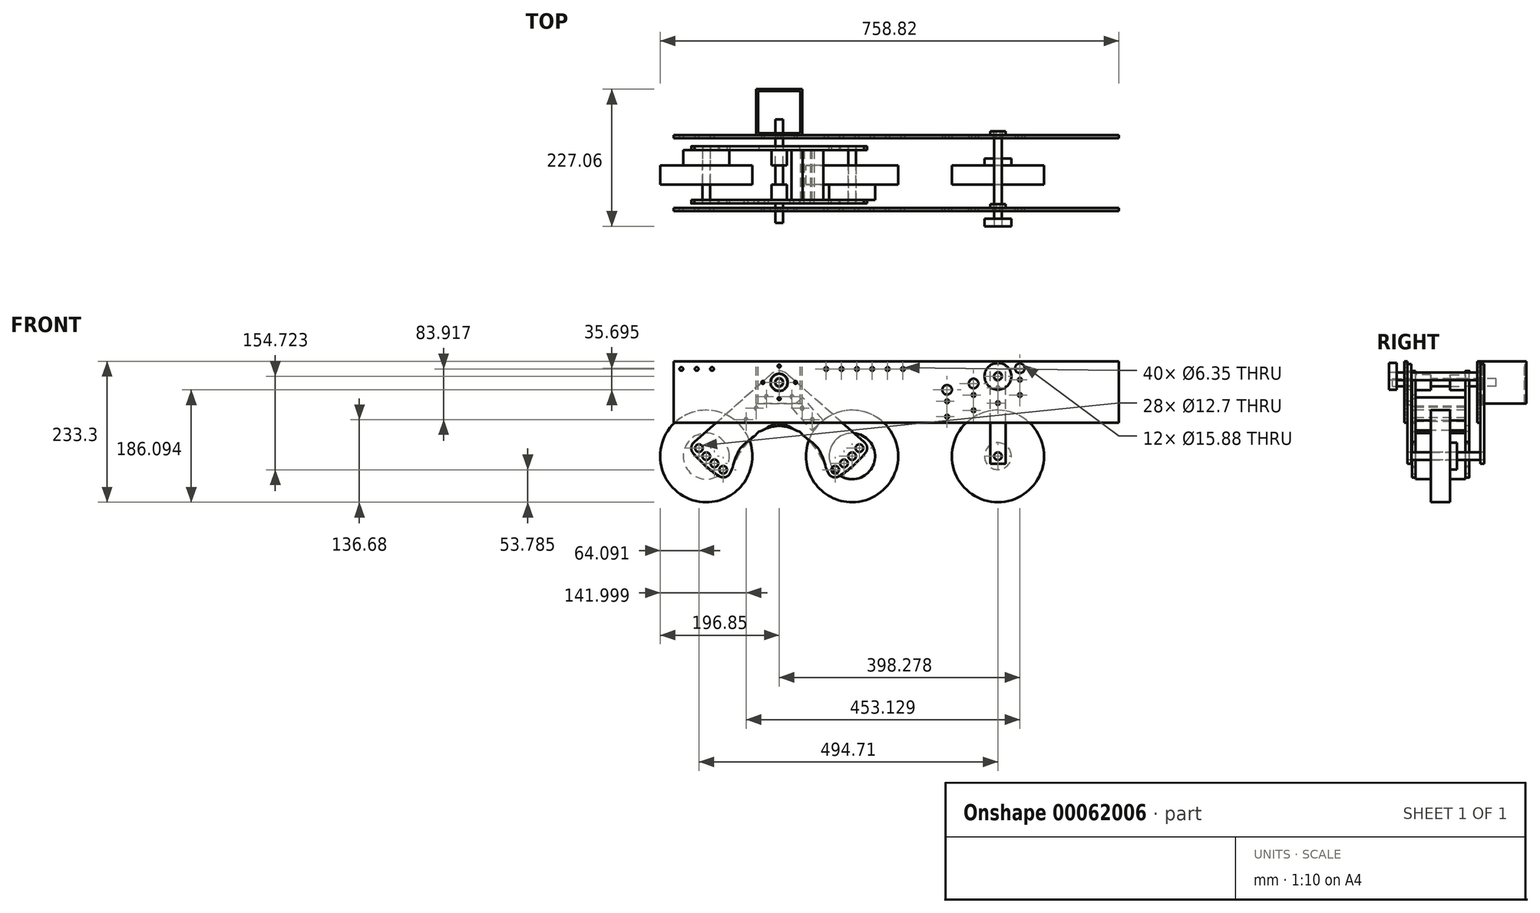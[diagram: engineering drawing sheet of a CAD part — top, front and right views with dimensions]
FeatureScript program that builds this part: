
annotation { "Feature Type Name" : "Feature", "Feature Type Description" : "" }
export const myFeature = defineFeature(function(context is Context, id is Id, definition is map)
    precondition{}
    {
        {
            var Q0;
            Q0=qCreatedBy(makeId("Front.planeOp"),FACE);
            var sketch = newSketch(context, id + "F0", { "sketchPlane" : qUnion([Q0])});
            skLineSegment(sketch, "E0", {"start": v(0, 0) * mm, "end": v(120.65, 122.17) * mm, "construction": true});
            skLineSegment(sketch, "E1", {"start": v(120.65, 122.17) * mm, "end": v(241.3, 0) * mm, "construction": true});
            skLineSegment(sketch, "E2", {"start": v(120.65, 122.17) * mm, "end": v(463.55, 122.17) * mm, "construction": true});
            skArc(sketch, "E3.0.startCap", {"start": v(120.65, 103.12) * mm, "mid": v(101.6, 122.17) * mm, "end": v(120.65, 141.22) * mm});
            skArc(sketch, "E3.0.endCap", {"start": v(463.55, 141.22) * mm, "mid": v(482.6, 122.17) * mm, "end": v(463.55, 103.12) * mm});
            skLineSegment(sketch, "E3.0.left", {"start": v(120.65, 141.22) * mm, "end": v(463.55, 141.22) * mm});
            skLineSegment(sketch, "E3.0.right", {"start": v(120.65, 103.12) * mm, "end": v(463.55, 103.12) * mm});
            skLineSegment(sketch, "E4", {"start": v(482.6, 132.33) * mm, "end": v(482.6, 0.02) * mm, "construction": true});
            skArc(sketch, "E5.0.startCap", {"start": v(469.9, 132.33) * mm, "mid": v(482.6, 145.03) * mm, "end": v(495.3, 132.33) * mm});
            skArc(sketch, "E5.0.endCap", {"start": v(495.3, 0.02) * mm, "mid": v(482.6, -12.68) * mm, "end": v(469.9, 0.02) * mm});
            skLineSegment(sketch, "E5.0.left", {"start": v(495.3, 132.33) * mm, "end": v(495.3, 0.02) * mm});
            skLineSegment(sketch, "E5.0.right", {"start": v(469.9, 132.33) * mm, "end": v(469.9, 0.02) * mm});
            skCircle(sketch, "E6", {"center": v(241.3, 0) * mm, "radius": 76.2 * mm});
            skCircle(sketch, "E7", {"center": v(0, 0) * mm, "radius": 76.2 * mm});
            skCircle(sketch, "E8", {"center": v(482.6, 0.02) * mm, "radius": 76.2 * mm});
            skCircle(sketch, "E9", {"center": v(0, 0) * mm, "radius": 6.35 * mm});
            skCircle(sketch, "E10", {"center": v(241.3, 0) * mm, "radius": 6.35 * mm});
            skCircle(sketch, "E11", {"center": v(482.6, 0.02) * mm, "radius": 6.35 * mm});
            skCircle(sketch, "E12", {"center": v(120.65, 122.17) * mm, "radius": 6.35 * mm});
            skCircle(sketch, "E13", {"center": v(0, 0) * mm, "radius": 38.1 * mm});
            skCircle(sketch, "E14", {"center": v(120.65, 122.17) * mm, "radius": 171.7 * mm, "construction": true});
            skCircle(sketch, "E15", {"center": v(13.43, -11.94) * mm, "radius": 6.35 * mm});
            skCircle(sketch, "E16", {"center": v(227.87, -11.94) * mm, "radius": 6.35 * mm});
            skCircle(sketch, "E17", {"center": v(213.26, -22.41) * mm, "radius": 6.35 * mm});
            skCircle(sketch, "E18", {"center": v(28.04, -22.41) * mm, "radius": 6.35 * mm});
            skLineSegment(sketch, "E19", {"start": v(13.43, -11.94) * mm, "end": v(120.65, 122.17) * mm, "construction": true});
            skLineSegment(sketch, "E20", {"start": v(120.65, 122.17) * mm, "end": v(28.04, -22.41) * mm, "construction": true});
            skLineSegment(sketch, "E21", {"start": v(120.65, 122.17) * mm, "end": v(213.26, -22.41) * mm, "construction": true});
            skLineSegment(sketch, "E22", {"start": v(120.65, 122.17) * mm, "end": v(227.87, -11.94) * mm, "construction": true});
            skLineSegment(sketch, "E23", {"start": v(120.65, 122.17) * mm, "end": v(253.4, 13.28) * mm, "construction": true});
            skLineSegment(sketch, "E24", {"start": v(120.65, 122.17) * mm, "end": v(-12.1, 13.28) * mm, "construction": true});
            skCircle(sketch, "E25", {"center": v(253.4, 13.28) * mm, "radius": 6.35 * mm});
            skCircle(sketch, "E26", {"center": v(-12.1, 13.28) * mm, "radius": 6.35 * mm});
            skCircle(sketch, "E27", {"center": v(120.65, 122.17) * mm, "radius": 19.05 * mm});
            skCircle(sketch, "E28", {"center": v(253.4, 13.28) * mm, "radius": 12.7 * mm, "construction": true});
            skLineSegment(sketch, "E29", {"start": v(261.1, 23.4) * mm, "end": v(133.27, 136.44) * mm});
            skCircle(sketch, "E30", {"center": v(-12.1, 13.28) * mm, "radius": 12.7 * mm, "construction": true});
            skLineSegment(sketch, "E31", {"start": v(120.65, 122.17) * mm, "end": v(263.23, 5.23) * mm, "construction": true});
            skArc(sketch, "E32", {"start": v(263.23, 5.23) * mm, "mid": v(120.65, -62.23) * mm, "end": v(-21.93, 5.23) * mm});
            skCircle(sketch, "E33", {"center": v(213.26, -22.41) * mm, "radius": 12.7 * mm, "construction": true});
            skCircle(sketch, "E34", {"center": v(28.04, -22.41) * mm, "radius": 12.7 * mm, "construction": true});
            skLineSegment(sketch, "E35", {"start": v(202.32, -28.86) * mm, "end": v(105, 111.3) * mm});
            skLineSegment(sketch, "E36", {"start": v(38.98, -28.86) * mm, "end": v(136.3, 111.3) * mm});
            skLineSegment(sketch, "E37", {"start": v(-19.8, 23.4) * mm, "end": v(108.03, 136.44) * mm});
            skLineSegment(sketch, "E38", {"start": v(303.84, -76.2) * mm, "end": v(-84, -76.2) * mm, "construction": true});
            skLineSegment(sketch, "E39", {"start": v(121.32, -76.2) * mm, "end": v(121.32, 40.64) * mm, "construction": true});
            skLineSegment(sketch, "E40", {"start": v(154.07, 40.64) * mm, "end": v(87.23, 40.64) * mm});
            skLineSegment(sketch, "E41.bottom", {"start": v(-53.97, 157.1) * mm, "end": v(682.62, 157.1) * mm});
            skLineSegment(sketch, "E41.top", {"start": v(-53.97, 55.5) * mm, "end": v(682.62, 55.5) * mm});
            skLineSegment(sketch, "E41.left", {"start": v(-53.98, 157.1) * mm, "end": v(-53.98, 55.5) * mm});
            skLineSegment(sketch, "E41.right", {"start": v(682.62, 157.1) * mm, "end": v(682.62, 55.5) * mm});
            skLineSegment(sketch, "E42", {"start": v(28.04, -22.41) * mm, "end": v(398.49, -22.41) * mm, "construction": true});
            skLineSegment(sketch, "E43", {"start": v(13.43, -11.94) * mm, "end": v(442.3, -11.94) * mm, "construction": true});
            skLineSegment(sketch, "E44", {"start": v(-12.1, 13.28) * mm, "end": v(518.93, 13.28) * mm, "construction": true});
            skLineSegment(sketch, "E45", {"start": v(398.49, -22.41) * mm, "end": v(398.49, 109.9) * mm, "construction": true});
            skLineSegment(sketch, "E46", {"start": v(442.3, -11.94) * mm, "end": v(442.3, 120.37) * mm, "construction": true});
            skLineSegment(sketch, "E47", {"start": v(518.93, 13.28) * mm, "end": v(518.93, 145.59) * mm, "construction": true});
            skLineSegment(sketch, "E48", {"start": v(0, 0) * mm, "end": v(482.6, 0) * mm, "construction": true});
            skLineSegment(sketch, "E49", {"start": v(482.6, 0) * mm, "end": v(482.6, 132.3) * mm, "construction": true});
            skSolve(sketch);
        }
        {
            var Q0;
            Q0=qCreatedBy(makeId("Front.planeOp"),FACE);
            var sketch = newSketch(context, id + "F1", { "sketchPlane" : qUnion([Q0])});
            skCircle(sketch, "E50.0", {"center": v(0, 0) * mm, "radius": 76.2 * mm});
            skCircle(sketch, "E51.0", {"center": v(241.3, 0) * mm, "radius": 76.2 * mm});
            skCircle(sketch, "E52.0", {"center": v(0, 0) * mm, "radius": 6.35 * mm});
            skCircle(sketch, "E53.0", {"center": v(241.3, 0) * mm, "radius": 6.35 * mm});
            skCircle(sketch, "E54.0", {"center": v(482.6, 0.02) * mm, "radius": 76.2 * mm});
            skCircle(sketch, "E55.0", {"center": v(482.6, 0.02) * mm, "radius": 6.35 * mm});
            skSolve(sketch);
        }
        {
            var Q0;
            Q0=makeQuery(id+"F1.imprint","IMPRINT",FACE,{"disambiguationData":[TD([[makeQuery(id+"F1.imprint","IMPRINT",EDGE,{"derivedFrom":sQuery(id+"F1.wireOp",EDGE,"E50.0")}),1.0]])]});
            var Q1;
            Q1=makeQuery(id+"F1.imprint","IMPRINT",FACE,{"disambiguationData":[TD([[makeQuery(id+"F1.imprint","IMPRINT",EDGE,{"derivedFrom":sQuery(id+"F1.wireOp",EDGE,"E51.0")}),1.0]])]});
            var Q2;
            Q2=makeQuery(id+"F1.imprint","IMPRINT",FACE,{"disambiguationData":[TD([[makeQuery(id+"F1.imprint","IMPRINT",EDGE,{"derivedFrom":sQuery(id+"F1.wireOp",EDGE,"E54.0")}),1.0]])]});
            extrude(context, id + "F2", {"entities" : qUnion([Q0, Q1, Q2]), "depth" : 31.75 * mm});
        }
        {
            var Q0;
            {var subQ0=sQuery(id+"F0.wireOp",EDGE,"E37");var subQ1=sQuery(id+"F0.wireOp",EDGE,"E7");var subQ2=makeQuery(id+"F0.imprint","INTERSECT",VERTEX,{"derivedFrom":[subQ1,subQ0]});Q0=makeQuery(id+"F0.imprint","IMPRINT",FACE,{"disambiguationData":[TD([[makeQuery(id+"F0.imprint","IMPRINT",EDGE,{"disambiguationData":[TD([[subQ2,-1.0]])],"derivedFrom":subQ1}),1.0]])]});}
            var sketch = newSketch(context, id + "F3", { "sketchPlane" : qUnion([Q0])});
            skCircle(sketch, "E56.0", {"center": v(0, 0) * mm, "radius": 38.1 * mm});
            skCircle(sketch, "E57.0", {"center": v(0, 0) * mm, "radius": 6.35 * mm});
            skSolve(sketch);
        }
        {
            var Q0;
            Q0=qSketchRegion(id+"F3",true);
            extrude(context, id + "F4", {"entities" : qUnion([Q0]), "oppositeDirection" : true, "depth" : 25.4 * mm});
        }
        {
            var Q0;
            Q0=makeQuery(id+"F2.opExtrude","CAP_FACE",FACE,{"disambiguationData":[OSD([sQuery(id+"F1.wireOp",EDGE,"E51.0")])],"isStart":false});
            var sketch = newSketch(context, id + "F5", { "sketchPlane" : qUnion([Q0])});
            skPoint(sketch, "E58.0", {"position": v(241.3, 0) * mm});
            skCircle(sketch, "E59", {"center": v(241.3, 0) * mm, "radius": 38.1 * mm});
            skCircle(sketch, "E60.0", {"center": v(241.3, 0) * mm, "radius": 6.35 * mm});
            skSolve(sketch);
        }
        {
            var Q0;
            Q0=qSketchRegion(id+"F5",true);
            extrude(context, id + "F6", {"entities" : qUnion([Q0]), "depth" : 25.4 * mm});
        }
        {
            var Q0;
            Q0=makeQuery(id+"F0.imprint","IMPRINT",FACE,{"disambiguationData":[TD([[makeQuery(id+"F0.imprint","IMPRINT",EDGE,{"derivedFrom":sQuery(id+"F0.wireOp",EDGE,"E12")}),1.0]])]});
            var Q1;
            Q1=makeQuery(id+"F4.opExtrude","CAP_FACE",FACE,{"disambiguationData":[OSD([sQuery(id+"F3.wireOp",EDGE,"E56.0")])],"isStart":false});
            var Q2;
            Q2=makeQuery(id+"F6.opExtrude","CAP_FACE",FACE,{"disambiguationData":[OSD([sQuery(id+"F5.wireOp",EDGE,"E59")])],"isStart":false});
            extrude(context, id + "F7", {"entities" : qUnion([Q0]), "endBound" : BoundingType.UP_TO_SURFACE, "oppositeDirection" : true, "endBoundEntityFace" : qUnion([Q1]), "depth" : 25.4 * mm, "hasSecondDirection" : true, "secondDirectionBound" : BoundingType.UP_TO_SURFACE, "secondDirectionOppositeDirection" : false, "secondDirectionBoundEntityFace" : qUnion([Q2]), "secondDirectionDepth" : 25.4 * mm});
        }
        {
            var Q0;
            Q0=makeQuery(id+"F7.opExtrude","CAP_FACE",FACE,{"disambiguationData":[OSD([sQuery(id+"F0.wireOp",EDGE,"E12")])],"isStart":true});
            var sketch = newSketch(context, id + "F8", { "sketchPlane" : qUnion([Q0])});
            skCircle(sketch, "E61", {"center": v(120.65, 122.17) * mm, "radius": 12.7 * mm});
            skSolve(sketch);
        }
        {
            var Q0;
            Q0=makeQuery(id+"F8.imprint","IMPRINT",FACE,{"disambiguationData":[TD([[makeQuery(id+"F8.imprint","IMPRINT",EDGE,{"derivedFrom":sQuery(id+"F8.wireOp",EDGE,"E61")}),1.0]])]});
            extrude(context, id + "F9", {"entities" : qUnion([Q0]), "oppositeDirection" : true, "depth" : 25.4 * mm});
        }
        {
            var Q0;
            Q0=makeQuery(id+"F7.opExtrude","CAP_FACE",FACE,{"disambiguationData":[OSD([sQuery(id+"F0.wireOp",EDGE,"E12")])],"isStart":false});
            var sketch = newSketch(context, id + "F10", { "sketchPlane" : qUnion([Q0])});
            skCircle(sketch, "E62.0", {"center": v(-120.65, 122.17) * mm, "radius": 12.7 * mm});
            skSolve(sketch);
        }
        {
            var Q0;
            Q0=makeQuery(id+"F10.imprint","IMPRINT",FACE,{"disambiguationData":[TD([[makeQuery(id+"F10.imprint","IMPRINT",EDGE,{"derivedFrom":sQuery(id+"F10.wireOp",EDGE,"E62.0")}),1.0]])]});
            extrude(context, id + "F11", {"entities" : qUnion([Q0]), "oppositeDirection" : true, "depth" : 25.4 * mm});
        }
        {
            var Q0;
            Q0=makeQuery(id+"F4.opExtrude","CAP_FACE",FACE,{"disambiguationData":[OSD([sQuery(id+"F3.wireOp",EDGE,"E56.0"),sQuery(id+"F3.wireOp",EDGE,"E57.0")])],"isStart":false});
            var sketch = newSketch(context, id + "F12", { "sketchPlane" : qUnion([Q0])});
            skLineSegment(sketch, "E63.0", {"start": v(-261.1, 23.4) * mm, "end": v(-133.27, 136.44) * mm});
            skArc(sketch, "E64.0", {"start": v(-133.27, 136.44) * mm, "mid": v(-120.65, 141.22) * mm, "end": v(-108.03, 136.44) * mm});
            skLineSegment(sketch, "E65.0", {"start": v(19.8, 23.4) * mm, "end": v(-108.03, 136.44) * mm});
            skLineSegment(sketch, "E66.0", {"start": v(-202.32, -28.86) * mm, "end": v(-154.07, 40.64) * mm, "construction": true});
            skLineSegment(sketch, "E67.0", {"start": v(-38.98, -28.86) * mm, "end": v(-87.23, 40.64) * mm, "construction": true});
            skLineSegment(sketch, "E68.0", {"start": v(-154.07, 40.64) * mm, "end": v(-87.23, 40.64) * mm, "construction": true});
            skArc(sketch, "E69.0", {"start": v(-202.32, -28.86) * mm, "mid": v(-210.32, -34.77) * mm, "end": v(-220.11, -33.1) * mm});
            skArc(sketch, "E70.0", {"start": v(-263.23, 5.23) * mm, "mid": v(-243.18, -15.64) * mm, "end": v(-220.11, -33.1) * mm});
            skArc(sketch, "E71.0", {"start": v(-263.23, 5.23) * mm, "mid": v(-266.02, 14.76) * mm, "end": v(-261.1, 23.4) * mm});
            skCircle(sketch, "E72.0", {"center": v(-253.4, 13.28) * mm, "radius": 6.35 * mm});
            skCircle(sketch, "E73.0", {"center": v(-241.3, 0) * mm, "radius": 6.35 * mm});
            skCircle(sketch, "E74.0", {"center": v(-227.87, -11.94) * mm, "radius": 6.35 * mm});
            skCircle(sketch, "E75.0", {"center": v(-213.26, -22.41) * mm, "radius": 6.35 * mm});
            skCircle(sketch, "E76.0", {"center": v(-120.65, 122.17) * mm, "radius": 6.35 * mm});
            skCircle(sketch, "E77.0", {"center": v(-28.04, -22.41) * mm, "radius": 6.35 * mm});
            skCircle(sketch, "E78.0", {"center": v(-13.43, -11.94) * mm, "radius": 6.35 * mm});
            skCircle(sketch, "E79.0", {"center": v(0, 0) * mm, "radius": 6.35 * mm});
            skCircle(sketch, "E80.0", {"center": v(12.1, 13.28) * mm, "radius": 6.35 * mm});
            skArc(sketch, "E81.0", {"start": v(19.8, 23.4) * mm, "mid": v(24.72, 14.76) * mm, "end": v(21.93, 5.23) * mm});
            skArc(sketch, "E82.trimOffspring", {"start": v(-21.19, -33.1) * mm, "mid": v(1.88, -15.64) * mm, "end": v(21.93, 5.23) * mm});
            skPoint(sketch, "E83.trimOffspring.end.orphan", {"position": v(-105, 111.3) * mm});
            skPoint(sketch, "E84.trimOffspring.end.orphan", {"position": v(-136.3, 111.3) * mm});
            skPoint(sketch, "E85", {"position": v(-120.65, 40.64) * mm});
            skLineSegment(sketch, "E86", {"start": v(-120.65, 40.64) * mm, "end": v(-120.65, 50.16) * mm, "construction": true});
            skFitSpline(sketch, "E87", {"points": [v(-154.07, 40.64) * mm, v(-120.65, 50.16) * mm, v(-87.23, 40.64) * mm], "startDerivative": vector(66.83, 28.57) * mm, "endDerivative": vector(66.83, -28.58) * mm});
            skArc(sketch, "E88", {"start": v(-38.98, -28.86) * mm, "mid": v(-30.98, -34.77) * mm, "end": v(-21.19, -33.1) * mm});
            skLineSegment(sketch, "E89", {"start": v(-178.2, 5.89) * mm, "end": v(-183.41, 9.5) * mm, "construction": true});
            skLineSegment(sketch, "E90", {"start": v(-63.1, 5.89) * mm, "end": v(-57.89, 9.5) * mm, "construction": true});
            skFitSpline(sketch, "E91", {"points": [v(-202.32, -28.86) * mm, v(-183.41, 9.5) * mm, v(-154.07, 40.64) * mm], "startDerivative": vector(32.6, 80.37) * mm, "endDerivative": vector(63.9, 58.64) * mm});
            skFitSpline(sketch, "E92", {"points": [v(-87.23, 40.64) * mm, v(-57.89, 9.5) * mm, v(-38.98, -28.86) * mm], "startDerivative": vector(63.9, -58.64) * mm, "endDerivative": vector(32.6, -80.37) * mm});
            skSolve(sketch);
        }
        {
            var Q0;
            Q0=qSketchRegion(id+"F12",true);
            extrude(context, id + "F13", {"entities" : qUnion([Q0]), "depth" : 6.05 * mm});
        }
        {
            var Q0;
            Q0=makeQuery(id+"F6.opExtrude","CAP_FACE",FACE,{"disambiguationData":[OSD([sQuery(id+"F5.wireOp",EDGE,"E59")])],"isStart":false});
            var sketch = newSketch(context, id + "F14", { "sketchPlane" : qUnion([Q0])});
            skLineSegment(sketch, "E93.0.0", {"start": v(108.03, 136.44) * mm, "end": v(-19.8, 23.4) * mm});
            skArc(sketch, "E93.0.1", {"start": v(-19.8, 23.4) * mm, "mid": v(-24.72, 14.76) * mm, "end": v(-21.93, 5.23) * mm});
            skArc(sketch, "E93.0.2", {"start": v(-21.93, 5.23) * mm, "mid": v(-1.88, -15.64) * mm, "end": v(21.19, -33.1) * mm});
            skArc(sketch, "E93.0.3", {"start": v(21.19, -33.1) * mm, "mid": v(30.98, -34.77) * mm, "end": v(38.98, -28.86) * mm});
            skFitSpline(sketch, "E93.0.4", {"points": [v(38.98, -28.86) * mm, v(44.41, -15.47) * mm, v(55.28, 11.32) * mm, v(76.58, 30.87) * mm, v(87.23, 40.64) * mm]});
            skFitSpline(sketch, "E93.0.5", {"points": [v(87.23, 40.64) * mm, v(98.37, 45.4) * mm, v(120.65, 54.93) * mm, v(142.93, 45.4) * mm, v(154.07, 40.64) * mm]});
            skFitSpline(sketch, "E93.0.6", {"points": [v(154.07, 40.64) * mm, v(164.72, 30.87) * mm, v(186.02, 11.32) * mm, v(196.89, -15.47) * mm, v(202.32, -28.86) * mm]});
            skArc(sketch, "E93.0.7", {"start": v(202.32, -28.86) * mm, "mid": v(210.32, -34.77) * mm, "end": v(220.11, -33.1) * mm});
            skArc(sketch, "E93.0.8", {"start": v(220.11, -33.1) * mm, "mid": v(243.18, -15.64) * mm, "end": v(263.23, 5.23) * mm});
            skArc(sketch, "E93.0.9", {"start": v(263.23, 5.23) * mm, "mid": v(266.02, 14.76) * mm, "end": v(261.1, 23.4) * mm});
            skLineSegment(sketch, "E93.0.10", {"start": v(261.1, 23.4) * mm, "end": v(133.27, 136.44) * mm});
            skArc(sketch, "E93.0.11", {"start": v(133.27, 136.44) * mm, "mid": v(120.65, 141.22) * mm, "end": v(108.03, 136.44) * mm});
            skCircle(sketch, "E94.0", {"center": v(-12.1, 13.28) * mm, "radius": 6.35 * mm});
            skCircle(sketch, "E95.0", {"center": v(0, 0) * mm, "radius": 6.35 * mm});
            skCircle(sketch, "E96.0", {"center": v(13.43, -11.94) * mm, "radius": 6.35 * mm});
            skCircle(sketch, "E97.0", {"center": v(28.04, -22.41) * mm, "radius": 6.35 * mm});
            skCircle(sketch, "E98.0", {"center": v(120.65, 122.17) * mm, "radius": 6.35 * mm});
            skCircle(sketch, "E99.0", {"center": v(213.26, -22.41) * mm, "radius": 6.35 * mm});
            skCircle(sketch, "E100.0", {"center": v(227.87, -11.94) * mm, "radius": 6.35 * mm});
            skCircle(sketch, "E101.0", {"center": v(241.3, 0) * mm, "radius": 6.35 * mm});
            skCircle(sketch, "E102.0", {"center": v(253.4, 13.28) * mm, "radius": 6.35 * mm});
            skCircle(sketch, "E103.0", {"center": v(120.65, 122.17) * mm, "radius": 12.7 * mm, "construction": true});
            skCircle(sketch, "E104", {"center": v(28.04, -22.41) * mm, "radius": 38.1 * mm, "construction": true});
            skCircle(sketch, "E105", {"center": v(-12.1, 13.28) * mm, "radius": 38.1 * mm, "construction": true});
            skLineSegment(sketch, "E106", {"start": v(16.14, -12.28) * mm, "end": v(131.4, 115.12) * mm, "construction": true});
            skLineSegment(sketch, "E107", {"start": v(-0.65, 2.66) * mm, "end": v(111.09, 130.53) * mm, "construction": true});
            skLineSegment(sketch, "E108", {"start": v(120.65, 122.17) * mm, "end": v(42.47, 34.24) * mm, "construction": true});
            skLineSegment(sketch, "E109", {"start": v(33.67, 41.93) * mm, "end": v(51.27, 26.55) * mm, "construction": true});
            skCircle(sketch, "E110", {"center": v(99.55, 98.44) * mm, "radius": 3.18 * mm});
            skCircle(sketch, "E111", {"center": v(82.68, 79.46) * mm, "radius": 3.18 * mm});
            skPoint(sketch, "E112.centerSnap0", {"position": v(55.22, 66.6) * mm});
            skCircle(sketch, "E113", {"center": v(65.8, 60.48) * mm, "radius": 3.18 * mm});
            skLineSegment(sketch, "E114", {"start": v(120.65, 122.17) * mm, "end": v(120.65, 50.16) * mm, "construction": true});
            skCircle(sketch, "E115.MirrorC", {"center": v(141.75, 98.44) * mm, "radius": 3.18 * mm});
            skCircle(sketch, "E116.MirrorC", {"center": v(158.62, 79.46) * mm, "radius": 3.18 * mm});
            skCircle(sketch, "E117.MirrorC", {"center": v(175.5, 60.48) * mm, "radius": 3.18 * mm});
            skSolve(sketch);
        }
        {
            var Q0;
            Q0=qSketchRegion(id+"F14",true);
            extrude(context, id + "F15", {"entities" : qUnion([Q0]), "depth" : 6.05 * mm});
        }
        {
            var Q0;
            Q0=makeQuery(id+"F15.opExtrude","CAP_FACE",FACE,{"disambiguationData":[OSD([sQuery(id+"F14.wireOp",EDGE,"E93.0.0"),sQuery(id+"F14.wireOp",EDGE,"E93.0.1"),sQuery(id+"F14.wireOp",EDGE,"E93.0.2"),sQuery(id+"F14.wireOp",EDGE,"E93.0.3"),sQuery(id+"F14.wireOp",EDGE,"E93.0.4"),sQuery(id+"F14.wireOp",EDGE,"E93.0.5"),sQuery(id+"F14.wireOp",EDGE,"E93.0.6"),sQuery(id+"F14.wireOp",EDGE,"E93.0.7"),sQuery(id+"F14.wireOp",EDGE,"E93.0.8"),sQuery(id+"F14.wireOp",EDGE,"E93.0.9"),sQuery(id+"F14.wireOp",EDGE,"E93.0.10"),sQuery(id+"F14.wireOp",EDGE,"E93.0.11"),sQuery(id+"F14.wireOp",EDGE,"E94.0"),sQuery(id+"F14.wireOp",EDGE,"E95.0"),sQuery(id+"F14.wireOp",EDGE,"E96.0"),sQuery(id+"F14.wireOp",EDGE,"E97.0"),sQuery(id+"F14.wireOp",EDGE,"E98.0"),sQuery(id+"F14.wireOp",EDGE,"E99.0"),sQuery(id+"F14.wireOp",EDGE,"E100.0"),sQuery(id+"F14.wireOp",EDGE,"E101.0"),sQuery(id+"F14.wireOp",EDGE,"E102.0"),sQuery(id+"F14.wireOp",EDGE,"E110"),sQuery(id+"F14.wireOp",EDGE,"E111"),sQuery(id+"F14.wireOp",EDGE,"E113"),sQuery(id+"F14.wireOp",EDGE,"E115.MirrorC"),sQuery(id+"F14.wireOp",EDGE,"E116.MirrorC"),sQuery(id+"F14.wireOp",EDGE,"E117.MirrorC")])],"isStart":false});
            cPlane(context, id + "F16", {"entities" : qUnion([Q0]), "cplaneType" : CPlaneType.OFFSET, "offset" : 107.95 * mm, "oppositeDirection" : true, "width" : 152.4 * mm, "height" : 152.4 * mm});
        }
        {
            var Q0;
            Q0=qCreatedBy(makeId("Right.planeOp"),FACE);
            var Q1;
            Q1=sQuery(id+"F12.wireOp",VERTEX,"E64.0.center");
            cPlane(context, id + "F17", {"entities" : qUnion([Q0, Q1]), "cplaneType" : CPlaneType.PLANE_POINT, "offset" : 152.4 * mm, "width" : 152.4 * mm, "height" : 152.4 * mm});
        }
        {
            var Q0;
            Q0=qCreatedBy(id+"F16.planeOp",FACE);
            var sketch = newSketch(context, id + "F18", { "sketchPlane" : qUnion([Q0])});
            skLineSegment(sketch, "E118.0", {"start": v(-53.97, 55.5) * mm, "end": v(682.62, 55.5) * mm});
            skLineSegment(sketch, "E119.0", {"start": v(-53.98, 157.1) * mm, "end": v(-53.98, 55.5) * mm});
            skLineSegment(sketch, "E120.0", {"start": v(-53.97, 157.1) * mm, "end": v(682.62, 157.1) * mm});
            skLineSegment(sketch, "E121.0", {"start": v(682.62, 157.1) * mm, "end": v(682.62, 55.5) * mm});
            skCircle(sketch, "E122.0", {"center": v(120.65, 122.17) * mm, "radius": 6.35 * mm});
            skLineSegment(sketch, "E123.rect.bottom", {"start": v(147.64, 149.16) * mm, "end": v(93.66, 149.16) * mm, "construction": true});
            skLineSegment(sketch, "E123.rect.top", {"start": v(147.64, 95.18) * mm, "end": v(93.66, 95.18) * mm, "construction": true});
            skLineSegment(sketch, "E123.rect.left", {"start": v(147.64, 149.16) * mm, "end": v(147.64, 95.18) * mm, "construction": true});
            skLineSegment(sketch, "E123.rect.right", {"start": v(93.66, 149.16) * mm, "end": v(93.66, 95.18) * mm, "construction": true});
            skCircle(sketch, "E124", {"center": v(120.65, 149.16) * mm, "radius": 2.43 * mm});
            skCircle(sketch, "E125", {"center": v(147.64, 122.17) * mm, "radius": 2.43 * mm});
            skCircle(sketch, "E126", {"center": v(120.65, 95.18) * mm, "radius": 2.43 * mm});
            skCircle(sketch, "E127", {"center": v(93.66, 122.17) * mm, "radius": 2.43 * mm});
            skPoint(sketch, "E128.0", {"position": v(518.93, 145.59) * mm});
            skPoint(sketch, "E129.0", {"position": v(482.6, 132.3) * mm});
            skPoint(sketch, "E130.0", {"position": v(442.3, 120.37) * mm});
            skPoint(sketch, "E131.0", {"position": v(398.49, 109.9) * mm});
            skCircle(sketch, "E132", {"center": v(518.93, 145.59) * mm, "radius": 7.94 * mm});
            skCircle(sketch, "E133", {"center": v(482.6, 132.3) * mm, "radius": 7.94 * mm});
            skCircle(sketch, "E134", {"center": v(442.3, 120.37) * mm, "radius": 7.94 * mm});
            skCircle(sketch, "E135", {"center": v(398.49, 109.9) * mm, "radius": 7.94 * mm});
            skLineSegment(sketch, "E136", {"start": v(518.93, 145.59) * mm, "end": v(518.93, 126.54) * mm, "construction": true});
            skPoint(sketch, "E137", {"position": v(482.6, 113.26) * mm});
            skPoint(sketch, "E138", {"position": v(442.3, 101.32) * mm});
            skPoint(sketch, "E139", {"position": v(398.49, 90.84) * mm});
            skLineSegment(sketch, "E140", {"start": v(482.6, 113.26) * mm, "end": v(482.6, 132.3) * mm, "construction": true});
            skLineSegment(sketch, "E141", {"start": v(442.3, 101.32) * mm, "end": v(442.3, 120.37) * mm, "construction": true});
            skLineSegment(sketch, "E142", {"start": v(398.49, 90.84) * mm, "end": v(398.49, 109.9) * mm, "construction": true});
            skPoint(sketch, "E143", {"position": v(518.93, 101.14) * mm});
            skPoint(sketch, "E144", {"position": v(482.6, 87.86) * mm});
            skPoint(sketch, "E145", {"position": v(442.3, 75.92) * mm});
            skPoint(sketch, "E146", {"position": v(398.49, 65.44) * mm});
            skLineSegment(sketch, "E147", {"start": v(518.93, 126.54) * mm, "end": v(518.93, 101.14) * mm, "construction": true});
            skLineSegment(sketch, "E148", {"start": v(482.6, 87.86) * mm, "end": v(482.6, 113.26) * mm, "construction": true});
            skLineSegment(sketch, "E149", {"start": v(442.3, 75.92) * mm, "end": v(442.3, 101.32) * mm, "construction": true});
            skLineSegment(sketch, "E150", {"start": v(398.49, 65.44) * mm, "end": v(398.49, 90.84) * mm, "construction": true});
            skCircle(sketch, "E151", {"center": v(518.93, 126.54) * mm, "radius": 3.18 * mm});
            skCircle(sketch, "E152", {"center": v(518.93, 101.14) * mm, "radius": 3.18 * mm});
            skCircle(sketch, "E153", {"center": v(482.6, 113.26) * mm, "radius": 3.18 * mm});
            skCircle(sketch, "E154", {"center": v(482.6, 87.86) * mm, "radius": 3.18 * mm});
            skCircle(sketch, "E155", {"center": v(442.3, 101.32) * mm, "radius": 3.17 * mm});
            skCircle(sketch, "E156", {"center": v(442.3, 75.92) * mm, "radius": 3.18 * mm});
            skCircle(sketch, "E157", {"center": v(398.49, 90.84) * mm, "radius": 3.18 * mm});
            skCircle(sketch, "E158", {"center": v(398.49, 65.44) * mm, "radius": 3.18 * mm});
            skCircle(sketch, "E159", {"center": v(-41.28, 144.4) * mm, "radius": 2.98 * mm});
            skCircle(sketch, "E160.1.0.0", {"center": v(-15.88, 144.4) * mm, "radius": 2.98 * mm});
            skCircle(sketch, "E160.2.0.0", {"center": v(9.52, 144.4) * mm, "radius": 2.98 * mm});
            skLineSegment(sketch, "E160.direction1", {"start": v(-41.28, 144.4) * mm, "end": v(-15.88, 144.4) * mm, "construction": true});
            skCircle(sketch, "E161", {"center": v(198.44, 144.4) * mm, "radius": 3.18 * mm});
            skCircle(sketch, "E162.1.0.0", {"center": v(223.84, 144.4) * mm, "radius": 3.18 * mm});
            skCircle(sketch, "E162.2.0.0", {"center": v(249.24, 144.4) * mm, "radius": 3.18 * mm});
            skCircle(sketch, "E162.3.0.0", {"center": v(274.64, 144.4) * mm, "radius": 3.18 * mm});
            skCircle(sketch, "E162.4.0.0", {"center": v(300.04, 144.4) * mm, "radius": 3.18 * mm});
            skCircle(sketch, "E162.5.0.0", {"center": v(325.44, 144.4) * mm, "radius": 3.18 * mm});
            skLineSegment(sketch, "E162.direction1", {"start": v(198.44, 144.4) * mm, "end": v(223.84, 144.4) * mm, "construction": true});
            skSolve(sketch);
        }
        {
            var Q0;
            Q0=qSketchRegion(id+"F18",true);
            extrude(context, id + "F19", {"entities" : qUnion([Q0]), "oppositeDirection" : true, "depth" : 4.94 * mm});
        }
        {
            var Q0;
            Q0=makeQuery(id+"F15.opExtrude","CAP_FACE",FACE,{"disambiguationData":[OSD([sQuery(id+"F14.wireOp",EDGE,"E93.0.0"),sQuery(id+"F14.wireOp",EDGE,"E93.0.1"),sQuery(id+"F14.wireOp",EDGE,"E93.0.2"),sQuery(id+"F14.wireOp",EDGE,"E93.0.3"),sQuery(id+"F14.wireOp",EDGE,"E93.0.4"),sQuery(id+"F14.wireOp",EDGE,"E93.0.5"),sQuery(id+"F14.wireOp",EDGE,"E93.0.6"),sQuery(id+"F14.wireOp",EDGE,"E93.0.7"),sQuery(id+"F14.wireOp",EDGE,"E93.0.8"),sQuery(id+"F14.wireOp",EDGE,"E93.0.9"),sQuery(id+"F14.wireOp",EDGE,"E93.0.10"),sQuery(id+"F14.wireOp",EDGE,"E93.0.11"),sQuery(id+"F14.wireOp",EDGE,"E94.0"),sQuery(id+"F14.wireOp",EDGE,"E95.0"),sQuery(id+"F14.wireOp",EDGE,"E96.0"),sQuery(id+"F14.wireOp",EDGE,"E97.0"),sQuery(id+"F14.wireOp",EDGE,"E98.0"),sQuery(id+"F14.wireOp",EDGE,"E99.0"),sQuery(id+"F14.wireOp",EDGE,"E100.0"),sQuery(id+"F14.wireOp",EDGE,"E101.0"),sQuery(id+"F14.wireOp",EDGE,"E102.0"),sQuery(id+"F14.wireOp",EDGE,"E110"),sQuery(id+"F14.wireOp",EDGE,"E111"),sQuery(id+"F14.wireOp",EDGE,"E113"),sQuery(id+"F14.wireOp",EDGE,"E115.MirrorC"),sQuery(id+"F14.wireOp",EDGE,"E116.MirrorC"),sQuery(id+"F14.wireOp",EDGE,"E117.MirrorC")])],"isStart":false});
            cPlane(context, id + "F20", {"entities" : qUnion([Q0]), "cplaneType" : CPlaneType.OFFSET, "offset" : 7.62 * mm, "width" : 152.4 * mm, "height" : 152.4 * mm});
        }
        {
            var Q0;
            Q0=qCreatedBy(id+"F20.planeOp",FACE);
            var sketch = newSketch(context, id + "F21", { "sketchPlane" : qUnion([Q0])});
            skLineSegment(sketch, "E163.0.0", {"start": v(682.62, 55.5) * mm, "end": v(682.62, 157.1) * mm});
            skLineSegment(sketch, "E163.0.1", {"start": v(682.62, 157.1) * mm, "end": v(-53.97, 157.1) * mm});
            skLineSegment(sketch, "E163.0.2", {"start": v(-53.98, 157.1) * mm, "end": v(-53.98, 55.5) * mm});
            skLineSegment(sketch, "E163.0.3", {"start": v(-53.97, 55.5) * mm, "end": v(682.62, 55.5) * mm});
            skCircle(sketch, "E164.1", {"center": v(120.65, 95.18) * mm, "radius": 2.43 * mm});
            skCircle(sketch, "E165.1", {"center": v(147.64, 122.17) * mm, "radius": 2.43 * mm});
            skCircle(sketch, "E165.2", {"center": v(120.65, 149.16) * mm, "radius": 2.43 * mm});
            skCircle(sketch, "E165.3", {"center": v(93.66, 122.17) * mm, "radius": 2.43 * mm});
            skPoint(sketch, "E166.0", {"position": v(398.49, 109.9) * mm});
            skPoint(sketch, "E167.0", {"position": v(442.3, 120.37) * mm});
            skPoint(sketch, "E168.0", {"position": v(482.6, 132.3) * mm});
            skPoint(sketch, "E169.0", {"position": v(518.93, 145.59) * mm});
            skPoint(sketch, "E170", {"position": v(398.49, 90.84) * mm});
            skPoint(sketch, "E171", {"position": v(442.3, 101.32) * mm});
            skPoint(sketch, "E172", {"position": v(482.6, 113.26) * mm});
            skPoint(sketch, "E173", {"position": v(518.93, 126.54) * mm});
            skLineSegment(sketch, "E174", {"start": v(398.49, 90.84) * mm, "end": v(398.49, 109.9) * mm, "construction": true});
            skLineSegment(sketch, "E175", {"start": v(442.3, 101.32) * mm, "end": v(442.3, 120.37) * mm, "construction": true});
            skLineSegment(sketch, "E176", {"start": v(482.6, 113.26) * mm, "end": v(482.6, 132.3) * mm, "construction": true});
            skLineSegment(sketch, "E177", {"start": v(518.93, 126.54) * mm, "end": v(518.93, 145.59) * mm, "construction": true});
            skCircle(sketch, "E178", {"center": v(398.49, 109.9) * mm, "radius": 7.94 * mm});
            skCircle(sketch, "E179", {"center": v(398.49, 90.84) * mm, "radius": 3.18 * mm});
            skCircle(sketch, "E180", {"center": v(442.3, 120.37) * mm, "radius": 7.94 * mm});
            skCircle(sketch, "E181", {"center": v(442.3, 101.32) * mm, "radius": 3.18 * mm});
            skCircle(sketch, "E182", {"center": v(482.6, 132.3) * mm, "radius": 7.94 * mm});
            skCircle(sketch, "E183", {"center": v(482.6, 113.26) * mm, "radius": 3.18 * mm});
            skCircle(sketch, "E184", {"center": v(518.93, 145.59) * mm, "radius": 7.94 * mm});
            skCircle(sketch, "E185", {"center": v(518.93, 126.54) * mm, "radius": 3.18 * mm});
            skLineSegment(sketch, "E186", {"start": v(398.49, 90.84) * mm, "end": v(398.49, 65.44) * mm, "construction": true});
            skPoint(sketch, "E187", {"position": v(442.3, 75.92) * mm});
            skPoint(sketch, "E188", {"position": v(482.6, 87.86) * mm});
            skPoint(sketch, "E189", {"position": v(518.93, 101.14) * mm});
            skLineSegment(sketch, "E190", {"start": v(442.3, 75.92) * mm, "end": v(442.3, 101.32) * mm, "construction": true});
            skLineSegment(sketch, "E191", {"start": v(482.6, 87.86) * mm, "end": v(482.6, 113.26) * mm, "construction": true});
            skLineSegment(sketch, "E192", {"start": v(518.93, 101.14) * mm, "end": v(518.93, 126.54) * mm, "construction": true});
            skCircle(sketch, "E193", {"center": v(398.49, 65.44) * mm, "radius": 3.18 * mm});
            skCircle(sketch, "E194", {"center": v(442.3, 75.92) * mm, "radius": 3.18 * mm});
            skCircle(sketch, "E195", {"center": v(482.6, 87.86) * mm, "radius": 3.18 * mm});
            skCircle(sketch, "E196", {"center": v(518.93, 101.14) * mm, "radius": 3.18 * mm});
            skCircle(sketch, "E197.0", {"center": v(-41.28, 144.4) * mm, "radius": 2.98 * mm});
            skCircle(sketch, "E198.0", {"center": v(-15.88, 144.4) * mm, "radius": 2.98 * mm});
            skCircle(sketch, "E199.0", {"center": v(9.52, 144.4) * mm, "radius": 2.98 * mm});
            skCircle(sketch, "E200.0", {"center": v(198.44, 144.4) * mm, "radius": 3.18 * mm});
            skCircle(sketch, "E201.0", {"center": v(223.84, 144.4) * mm, "radius": 3.18 * mm});
            skCircle(sketch, "E202.0", {"center": v(249.24, 144.4) * mm, "radius": 3.18 * mm});
            skCircle(sketch, "E203.0", {"center": v(274.64, 144.4) * mm, "radius": 3.18 * mm});
            skCircle(sketch, "E204.0", {"center": v(300.04, 144.4) * mm, "radius": 3.18 * mm});
            skCircle(sketch, "E205.0", {"center": v(325.44, 144.4) * mm, "radius": 3.18 * mm});
            skPoint(sketch, "E206.0", {"position": v(120.65, 122.17) * mm});
            skCircle(sketch, "E207", {"center": v(120.65, 122.17) * mm, "radius": 14.29 * mm});
            skSolve(sketch);
        }
        {
            var Q0;
            Q0=qSketchRegion(id+"F21",true);
            extrude(context, id + "F22", {"entities" : qUnion([Q0]), "depth" : 4.94 * mm});
        }
        {
            var Q0;
            {var subQ1=sQuery(id+"F0.wireOp",EDGE,"E5.0.endCap");Q0=makeQuery(id+"F0.imprint","IMPRINT",FACE,{"disambiguationData":[TD([[makeQuery(id+"F0.imprint","IMPRINT",EDGE,{"derivedFrom":subQ1}),1.0]])]});}
            var sketch = newSketch(context, id + "F23", { "sketchPlane" : qUnion([Q0])});
            skPoint(sketch, "E208.0", {"position": v(482.6, 0.02) * mm});
            skCircle(sketch, "E209", {"center": v(482.6, 0.02) * mm, "radius": 22.23 * mm});
            skSolve(sketch);
        }
        {
            var Q0;
            Q0=qSketchRegion(id+"F23",true);
            extrude(context, id + "F24", {"entities" : qUnion([Q0]), "oppositeDirection" : true, "depth" : 11.43 * mm});
        }
        {
            var Q0;
            Q0=sQuery(id+"F0.wireOp",VERTEX,"E4.end");
            var Q1;
            Q1=makeQuery(id+"F22.opExtrude","SWEPT_FACE",FACE,{"disambiguationData":[OSD([sQuery(id+"F21.wireOp",EDGE,"E163.0.3")])]});
            cPlane(context, id + "F25", {"entities" : qUnion([Q0, Q1]), "cplaneType" : CPlaneType.PLANE_POINT, "offset" : 152.4 * mm, "width" : 152.4 * mm, "height" : 152.4 * mm});
        }
        {
            var Q0;
            Q0=qCreatedBy(id+"F25.planeOp",FACE);
            var sketch = newSketch(context, id + "F26", { "sketchPlane" : qUnion([Q0])});
            skLineSegment(sketch, "E210", {"start": v(482.6, -30.16) * mm, "end": v(482.6, 61.91) * mm, "construction": true});
            skLineSegment(sketch, "E211.bottom", {"start": v(469.9, -49.7) * mm, "end": v(495.3, -49.7) * mm});
            skLineSegment(sketch, "E211.top", {"start": v(469.9, -56.05) * mm, "end": v(495.3, -56.05) * mm});
            skLineSegment(sketch, "E211.left", {"start": v(469.9, -49.7) * mm, "end": v(469.9, -56.05) * mm});
            skLineSegment(sketch, "E211.right", {"start": v(495.3, -49.7) * mm, "end": v(495.3, -56.05) * mm});
            skLineSegment(sketch, "E212.bottom", {"start": v(469.9, 64.47) * mm, "end": v(495.3, 64.47) * mm});
            skLineSegment(sketch, "E212.top", {"start": v(469.9, 70.82) * mm, "end": v(495.3, 70.82) * mm});
            skLineSegment(sketch, "E212.left", {"start": v(469.9, 64.47) * mm, "end": v(469.9, 70.82) * mm});
            skLineSegment(sketch, "E212.right", {"start": v(495.3, 64.47) * mm, "end": v(495.3, 70.82) * mm});
            skLineSegment(sketch, "E213.0", {"start": v(-53.97, -49.7) * mm, "end": v(682.62, -49.7) * mm, "construction": true});
            skLineSegment(sketch, "E214.0", {"start": v(-53.97, 70.82) * mm, "end": v(682.62, 70.82) * mm, "construction": true});
            skSolve(sketch);
        }
        {
            var Q0;
            Q0=qSketchRegion(id+"F26",true);
            extrude(context, id + "F27", {"entities" : qUnion([Q0]), "depth" : 12.7 * mm, "hasSecondDirection" : true, "secondDirectionOppositeDirection" : true, "secondDirectionDepth" : 152.4 * mm});
        }
        {
            var Q0;
            Q0=makeQuery(id+"F27.opExtrude","SWEPT_FACE",FACE,{"disambiguationData":[OSD([sQuery(id+"F26.wireOp",EDGE,"E212.top")])]});
            var sketch = newSketch(context, id + "F28", { "sketchPlane" : qUnion([Q0])});
            skLineSegment(sketch, "E215", {"start": v(482.6, -12.68) * mm, "end": v(482.6, 152.42) * mm, "construction": true});
            skCircle(sketch, "E216", {"center": v(482.6, 0.02) * mm, "radius": 6.35 * mm});
            skPoint(sketch, "E217.0", {"position": v(482.6, 132.33) * mm});
            skCircle(sketch, "E218.0", {"center": v(482.6, 132.3) * mm, "radius": 7.94 * mm});
            skCircle(sketch, "E219.0", {"center": v(482.6, 113.26) * mm, "radius": 3.18 * mm});
            skCircle(sketch, "E220.0", {"center": v(482.6, 87.86) * mm, "radius": 3.18 * mm});
            skSolve(sketch);
        }
        {
            var Q0;
            Q0=qSketchRegion(id+"F28",true);
            var Q1;
            Q1=makeQuery(id+"F27.opExtrude","SWEPT_FACE",FACE,{"disambiguationData":[OSD([sQuery(id+"F26.wireOp",EDGE,"E211.top")])]});
            extrude(context, id + "F29", {"entities" : qUnion([Q0]), "operationType" : NewBodyOperationType.REMOVE, "endBound" : BoundingType.UP_TO_SURFACE, "oppositeDirection" : true, "endBoundEntityFace" : qUnion([Q1]), "depth" : 25.4 * mm});
        }
        {
            var Q0;
            Q0=makeQuery(id+"F19.opExtrude","SWEPT_FACE",FACE,{"disambiguationData":[OSD([sQuery(id+"F18.wireOp",EDGE,"E120.0")])]});
            var sketch = newSketch(context, id + "F30", { "sketchPlane" : qUnion([Q0])});
            skLineSegment(sketch, "E221.bottom", {"start": v(158.75, 49.7) * mm, "end": v(82.55, 49.7) * mm});
            skLineSegment(sketch, "E221.top", {"start": v(158.75, 125.9) * mm, "end": v(82.55, 125.9) * mm});
            skLineSegment(sketch, "E221.left", {"start": v(158.75, 49.7) * mm, "end": v(158.75, 125.9) * mm});
            skLineSegment(sketch, "E221.right", {"start": v(82.55, 49.7) * mm, "end": v(82.55, 125.9) * mm});
            skPoint(sketch, "E222", {"position": v(120.65, 49.7) * mm});
            skLineSegment(sketch, "E223.0", {"start": v(127, 49.7) * mm, "end": v(114.3, 49.7) * mm, "construction": true});
            skLineSegment(sketch, "E224.0", {"start": v(155.57, 52.87) * mm, "end": v(155.57, 122.72) * mm});
            skLineSegment(sketch, "E224.1", {"start": v(155.57, 52.87) * mm, "end": v(85.73, 52.87) * mm});
            skLineSegment(sketch, "E224.2", {"start": v(85.73, 52.87) * mm, "end": v(85.73, 122.72) * mm});
            skLineSegment(sketch, "E224.3", {"start": v(155.57, 122.72) * mm, "end": v(85.73, 122.72) * mm});
            skLineSegment(sketch, "E225.0", {"start": v(-53.97, 49.7) * mm, "end": v(682.62, 49.7) * mm, "construction": true});
            skSolve(sketch);
        }
        {
            var Q0;
            Q0=qSketchRegion(id+"F30",true);
            extrude(context, id + "F31", {"entities" : qUnion([Q0]), "oppositeDirection" : true, "depth" : 69.85 * mm});
        }
        {
            var Q0;
            Q0=makeQuery(id+"F31.opExtrude","SWEPT_FACE",FACE,{"disambiguationData":[OSD([sQuery(id+"F30.wireOp",EDGE,"E221.top")])]});
            var sketch = newSketch(context, id + "F32", { "sketchPlane" : qUnion([Q0])});
            skCircle(sketch, "E226.0", {"center": v(-120.65, 149.16) * mm, "radius": 2.43 * mm});
            skCircle(sketch, "E227.0", {"center": v(-147.64, 122.17) * mm, "radius": 2.43 * mm});
            skCircle(sketch, "E228.0", {"center": v(-120.65, 95.18) * mm, "radius": 2.43 * mm});
            skCircle(sketch, "E229.0", {"center": v(-93.66, 122.17) * mm, "radius": 2.43 * mm});
            skCircle(sketch, "E230", {"center": v(-120.65, 122.17) * mm, "radius": 7.94 * mm});
            skSolve(sketch);
        }
        {
            var Q0;
            Q0=qSketchRegion(id+"F32",true);
            var Q1;
            Q1=makeQuery(id+"F31.opExtrude","SWEPT_FACE",FACE,{"disambiguationData":[OSD([sQuery(id+"F30.wireOp",EDGE,"E221.bottom")])]});
            extrude(context, id + "F33", {"entities" : qUnion([Q0]), "operationType" : NewBodyOperationType.REMOVE, "endBound" : BoundingType.UP_TO_SURFACE, "oppositeDirection" : true, "endBoundEntityFace" : qUnion([Q1]), "depth" : 25.4 * mm});
        }
        {
            var Q0;
            Q0=qCreatedBy(makeId("Front.planeOp"),FACE);
            var sketch = newSketch(context, id + "F34", { "sketchPlane" : qUnion([Q0])});
            skCircle(sketch, "E231.0", {"center": v(482.6, 132.3) * mm, "radius": 6.35 * mm});
            skSolve(sketch);
        }
        {
            var Q0;
            Q0=qSketchRegion(id+"F34",true);
            var Q1;
            Q1=makeQuery(id+"F27.opExtrude","SWEPT_FACE",FACE,{"disambiguationData":[OSD([sQuery(id+"F26.wireOp",EDGE,"E211.top")])]});
            var Q2;
            Q2=makeQuery(id+"F22.opExtrude","CAP_FACE",FACE,{"disambiguationData":[OSD([sQuery(id+"F21.wireOp",EDGE,"E163.0.0"),sQuery(id+"F21.wireOp",EDGE,"E163.0.1"),sQuery(id+"F21.wireOp",EDGE,"E163.0.2"),sQuery(id+"F21.wireOp",EDGE,"E163.0.3"),sQuery(id+"F21.wireOp",EDGE,"E164.1"),sQuery(id+"F21.wireOp",EDGE,"E165.1"),sQuery(id+"F21.wireOp",EDGE,"E165.2"),sQuery(id+"F21.wireOp",EDGE,"E165.3"),sQuery(id+"F21.wireOp",EDGE,"E178"),sQuery(id+"F21.wireOp",EDGE,"E179"),sQuery(id+"F21.wireOp",EDGE,"E180"),sQuery(id+"F21.wireOp",EDGE,"E181"),sQuery(id+"F21.wireOp",EDGE,"E182"),sQuery(id+"F21.wireOp",EDGE,"E183"),sQuery(id+"F21.wireOp",EDGE,"E184"),sQuery(id+"F21.wireOp",EDGE,"E185"),sQuery(id+"F21.wireOp",EDGE,"E193"),sQuery(id+"F21.wireOp",EDGE,"E194"),sQuery(id+"F21.wireOp",EDGE,"E195"),sQuery(id+"F21.wireOp",EDGE,"E196"),sQuery(id+"F21.wireOp",EDGE,"E197.0"),sQuery(id+"F21.wireOp",EDGE,"E198.0"),sQuery(id+"F21.wireOp",EDGE,"E199.0"),sQuery(id+"F21.wireOp",EDGE,"E200.0"),sQuery(id+"F21.wireOp",EDGE,"E201.0"),sQuery(id+"F21.wireOp",EDGE,"E202.0"),sQuery(id+"F21.wireOp",EDGE,"E203.0"),sQuery(id+"F21.wireOp",EDGE,"E204.0"),sQuery(id+"F21.wireOp",EDGE,"E205.0"),sQuery(id+"F21.wireOp",EDGE,"E207")])],"isStart":false});
            extrude(context, id + "F35", {"entities" : qUnion([Q0]), "endBound" : BoundingType.UP_TO_SURFACE, "oppositeDirection" : true, "endBoundEntityFace" : qUnion([Q1]), "depth" : 25.4 * mm, "hasSecondDirection" : true, "secondDirectionBound" : BoundingType.UP_TO_SURFACE, "secondDirectionOppositeDirection" : false, "secondDirectionBoundEntityFace" : qUnion([Q2]), "secondDirectionDepth" : 95.25 * mm});
        }
        {
            var Q0;
            Q0=makeQuery(id+"F35.opExtrude","CAP_FACE",FACE,{"disambiguationData":[OSD([sQuery(id+"F34.wireOp",EDGE,"E231.0")])],"isStart":true});
            extrude(context, id + "F36", {"entities" : qUnion([Q0]), "operationType" : NewBodyOperationType.ADD, "depth" : 25.4 * mm});
        }
        {
            var Q0;
            Q0=makeQuery(id+"F36.opExtrude","CAP_FACE",FACE,{"disambiguationData":[OSD([sQuery(id+"F34.wireOp",EDGE,"E231.0")])],"isStart":false});
            var sketch = newSketch(context, id + "F37", { "sketchPlane" : qUnion([Q0])});
            skCircle(sketch, "E232", {"center": v(482.6, 132.3) * mm, "radius": 22.23 * mm});
            skPoint(sketch, "E233.0", {"position": v(482.6, 132.33) * mm});
            skCircle(sketch, "E234.0", {"center": v(482.6, 132.3) * mm, "radius": 6.35 * mm});
            skSolve(sketch);
        }
        {
            var Q0;
            Q0=qSketchRegion(id+"F37",true);
            extrude(context, id + "F38", {"entities" : qUnion([Q0]), "oppositeDirection" : true, "depth" : 12.7 * mm});
        }
        {
            var Q0;
            Q0=makeQuery(id+"F7.opExtrude","CAP_FACE",FACE,{"disambiguationData":[OSD([sQuery(id+"F0.wireOp",EDGE,"E12")])],"isStart":true});
            extrude(context, id + "F39", {"entities" : qUnion([Q0]), "operationType" : NewBodyOperationType.ADD, "depth" : 38.1 * mm});
        }
        {
            var Q0;
            Q0=makeQuery(id+"F27.opExtrude","SWEPT_FACE",FACE,{"disambiguationData":[OSD([sQuery(id+"F26.wireOp",EDGE,"E212.top")])]});
            var sketch = newSketch(context, id + "F40", { "sketchPlane" : qUnion([Q0])});
            skCircle(sketch, "E235.0", {"center": v(482.6, 0.02) * mm, "radius": 6.35 * mm});
            skSolve(sketch);
        }
        {
            var Q0;
            Q0=qSketchRegion(id+"F40",true);
            var Q1;
            Q1=makeQuery(id+"F27.opExtrude","SWEPT_FACE",FACE,{"disambiguationData":[OSD([sQuery(id+"F26.wireOp",EDGE,"E211.top")])]});
            extrude(context, id + "F41", {"entities" : qUnion([Q0]), "endBound" : BoundingType.UP_TO_SURFACE, "oppositeDirection" : true, "endBoundEntityFace" : qUnion([Q1]), "depth" : 25.4 * mm});
        }
        {
            var Q0;
            Q0=makeQuery(id+"F15.opExtrude","CAP_FACE",FACE,{"disambiguationData":[OSD([sQuery(id+"F14.wireOp",EDGE,"E93.0.0"),sQuery(id+"F14.wireOp",EDGE,"E93.0.1"),sQuery(id+"F14.wireOp",EDGE,"E93.0.2"),sQuery(id+"F14.wireOp",EDGE,"E93.0.3"),sQuery(id+"F14.wireOp",EDGE,"E93.0.4"),sQuery(id+"F14.wireOp",EDGE,"E93.0.5"),sQuery(id+"F14.wireOp",EDGE,"E93.0.6"),sQuery(id+"F14.wireOp",EDGE,"E93.0.7"),sQuery(id+"F14.wireOp",EDGE,"E93.0.8"),sQuery(id+"F14.wireOp",EDGE,"E93.0.9"),sQuery(id+"F14.wireOp",EDGE,"E93.0.10"),sQuery(id+"F14.wireOp",EDGE,"E93.0.11"),sQuery(id+"F14.wireOp",EDGE,"E94.0"),sQuery(id+"F14.wireOp",EDGE,"E95.0"),sQuery(id+"F14.wireOp",EDGE,"E96.0"),sQuery(id+"F14.wireOp",EDGE,"E97.0"),sQuery(id+"F14.wireOp",EDGE,"E98.0"),sQuery(id+"F14.wireOp",EDGE,"E99.0"),sQuery(id+"F14.wireOp",EDGE,"E100.0"),sQuery(id+"F14.wireOp",EDGE,"E101.0"),sQuery(id+"F14.wireOp",EDGE,"E102.0"),sQuery(id+"F14.wireOp",EDGE,"E110"),sQuery(id+"F14.wireOp",EDGE,"E111"),sQuery(id+"F14.wireOp",EDGE,"E113"),sQuery(id+"F14.wireOp",EDGE,"E115.MirrorC"),sQuery(id+"F14.wireOp",EDGE,"E116.MirrorC"),sQuery(id+"F14.wireOp",EDGE,"E117.MirrorC")])],"isStart":false});
            var sketch = newSketch(context, id + "F42", { "sketchPlane" : qUnion([Q0])});
            skCircle(sketch, "E236.0", {"center": v(0, 0) * mm, "radius": 6.35 * mm});
            skCircle(sketch, "E237.0", {"center": v(241.3, 0) * mm, "radius": 6.35 * mm});
            skSolve(sketch);
        }
        {
            var Q0;
            Q0=qSketchRegion(id+"F42",true);
            var Q1;
            Q1=makeQuery(id+"F13.opExtrude","CAP_FACE",FACE,{"disambiguationData":[OSD([sQuery(id+"F12.wireOp",EDGE,"E63.0"),sQuery(id+"F12.wireOp",EDGE,"E64.0"),sQuery(id+"F12.wireOp",EDGE,"E65.0"),sQuery(id+"F12.wireOp",EDGE,"E69.0"),sQuery(id+"F12.wireOp",EDGE,"E70.0"),sQuery(id+"F12.wireOp",EDGE,"E71.0"),sQuery(id+"F12.wireOp",EDGE,"E72.0"),sQuery(id+"F12.wireOp",EDGE,"E73.0"),sQuery(id+"F12.wireOp",EDGE,"E74.0"),sQuery(id+"F12.wireOp",EDGE,"E75.0"),sQuery(id+"F12.wireOp",EDGE,"E76.0"),sQuery(id+"F12.wireOp",EDGE,"E77.0"),sQuery(id+"F12.wireOp",EDGE,"E78.0"),sQuery(id+"F12.wireOp",EDGE,"E79.0"),sQuery(id+"F12.wireOp",EDGE,"E80.0"),sQuery(id+"F12.wireOp",EDGE,"E81.0"),sQuery(id+"F12.wireOp",EDGE,"E82.trimOffspring"),sQuery(id+"F12.wireOp",EDGE,"E87"),sQuery(id+"F12.wireOp",EDGE,"E88"),sQuery(id+"F12.wireOp",EDGE,"E91"),sQuery(id+"F12.wireOp",EDGE,"E92")])],"isStart":false});
            extrude(context, id + "F43", {"entities" : qUnion([Q0]), "endBound" : BoundingType.UP_TO_SURFACE, "oppositeDirection" : true, "endBoundEntityFace" : qUnion([Q1]), "depth" : 25.4 * mm});
        }
        {
            var Q0;
            Q0=makeQuery(id+"F7.opExtrude","CAP_FACE",FACE,{"disambiguationData":[OSD([sQuery(id+"F0.wireOp",EDGE,"E12")])],"isStart":false});
            extrude(context, id + "F44", {"entities" : qUnion([Q0]), "depth" : 50.8 * mm});
        }
        {
            var Q0;
            Q0=makeQuery(id+"F15.opExtrude","CAP_FACE",FACE,{"disambiguationData":[OSD([sQuery(id+"F14.wireOp",EDGE,"E93.0.0"),sQuery(id+"F14.wireOp",EDGE,"E93.0.1"),sQuery(id+"F14.wireOp",EDGE,"E93.0.2"),sQuery(id+"F14.wireOp",EDGE,"E93.0.3"),sQuery(id+"F14.wireOp",EDGE,"E93.0.4"),sQuery(id+"F14.wireOp",EDGE,"E93.0.5"),sQuery(id+"F14.wireOp",EDGE,"E93.0.6"),sQuery(id+"F14.wireOp",EDGE,"E93.0.7"),sQuery(id+"F14.wireOp",EDGE,"E93.0.8"),sQuery(id+"F14.wireOp",EDGE,"E93.0.9"),sQuery(id+"F14.wireOp",EDGE,"E93.0.10"),sQuery(id+"F14.wireOp",EDGE,"E93.0.11"),sQuery(id+"F14.wireOp",EDGE,"E94.0"),sQuery(id+"F14.wireOp",EDGE,"E95.0"),sQuery(id+"F14.wireOp",EDGE,"E96.0"),sQuery(id+"F14.wireOp",EDGE,"E97.0"),sQuery(id+"F14.wireOp",EDGE,"E98.0"),sQuery(id+"F14.wireOp",EDGE,"E99.0"),sQuery(id+"F14.wireOp",EDGE,"E100.0"),sQuery(id+"F14.wireOp",EDGE,"E101.0"),sQuery(id+"F14.wireOp",EDGE,"E102.0"),sQuery(id+"F14.wireOp",EDGE,"E110"),sQuery(id+"F14.wireOp",EDGE,"E111"),sQuery(id+"F14.wireOp",EDGE,"E113"),sQuery(id+"F14.wireOp",EDGE,"E115.MirrorC"),sQuery(id+"F14.wireOp",EDGE,"E116.MirrorC"),sQuery(id+"F14.wireOp",EDGE,"E117.MirrorC")])],"isStart":true});
            var sketch = newSketch(context, id + "F45", { "sketchPlane" : qUnion([Q0])});
            skLineSegment(sketch, "E238", {"start": v(-175.5, 60.48) * mm, "end": v(-158.62, 79.46) * mm, "construction": true});
            skLineSegment(sketch, "E239", {"start": v(-193.43, 59.43) * mm, "end": v(-159.68, 97.4) * mm});
            skLineSegment(sketch, "E240", {"start": v(-159.68, 97.4) * mm, "end": v(-140.7, 80.51) * mm});
            skLineSegment(sketch, "E241", {"start": v(-140.7, 80.51) * mm, "end": v(-174.45, 42.55) * mm});
            skLineSegment(sketch, "E242", {"start": v(-174.45, 42.55) * mm, "end": v(-193.43, 59.43) * mm});
            skLineSegment(sketch, "E243", {"start": v(-157.57, 61.53) * mm, "end": v(-167.06, 69.97) * mm, "construction": true});
            skPoint(sketch, "E243.endSnap0", {"position": v(-167.06, 69.97) * mm});
            skLineSegment(sketch, "E244", {"start": v(-183.94, 50.99) * mm, "end": v(-175.5, 60.48) * mm, "construction": true});
            skCircle(sketch, "E245.0", {"center": v(-175.5, 60.48) * mm, "radius": 3.18 * mm});
            skCircle(sketch, "E246.0", {"center": v(-158.62, 79.46) * mm, "radius": 3.18 * mm});
            skSolve(sketch);
        }
        {
            var Q0;
            Q0=qSketchRegion(id+"F45",true);
            var Q1;
            Q1=makeQuery(id+"F13.opExtrude","CAP_FACE",FACE,{"disambiguationData":[OSD([sQuery(id+"F12.wireOp",EDGE,"E63.0"),sQuery(id+"F12.wireOp",EDGE,"E64.0"),sQuery(id+"F12.wireOp",EDGE,"E65.0"),sQuery(id+"F12.wireOp",EDGE,"E69.0"),sQuery(id+"F12.wireOp",EDGE,"E70.0"),sQuery(id+"F12.wireOp",EDGE,"E71.0"),sQuery(id+"F12.wireOp",EDGE,"E72.0"),sQuery(id+"F12.wireOp",EDGE,"E73.0"),sQuery(id+"F12.wireOp",EDGE,"E74.0"),sQuery(id+"F12.wireOp",EDGE,"E75.0"),sQuery(id+"F12.wireOp",EDGE,"E76.0"),sQuery(id+"F12.wireOp",EDGE,"E77.0"),sQuery(id+"F12.wireOp",EDGE,"E78.0"),sQuery(id+"F12.wireOp",EDGE,"E79.0"),sQuery(id+"F12.wireOp",EDGE,"E80.0"),sQuery(id+"F12.wireOp",EDGE,"E81.0"),sQuery(id+"F12.wireOp",EDGE,"E82.trimOffspring"),sQuery(id+"F12.wireOp",EDGE,"E87"),sQuery(id+"F12.wireOp",EDGE,"E88"),sQuery(id+"F12.wireOp",EDGE,"E91"),sQuery(id+"F12.wireOp",EDGE,"E92")])],"isStart":true});
            extrude(context, id + "F46", {"entities" : qUnion([Q0]), "endBound" : BoundingType.UP_TO_SURFACE, "endBoundEntityFace" : qUnion([Q1]), "depth" : 25.4 * mm});
        }
    });
